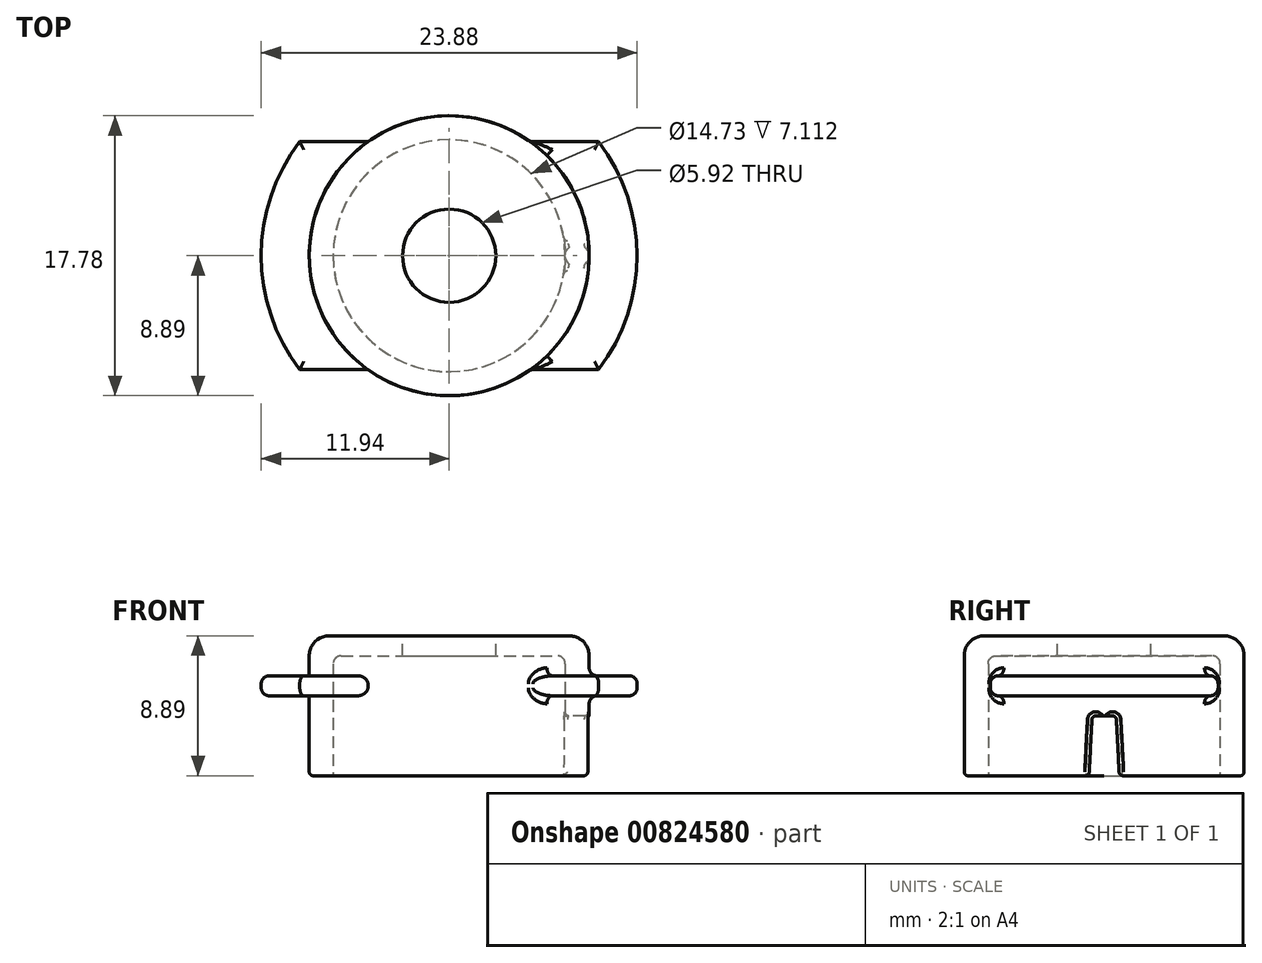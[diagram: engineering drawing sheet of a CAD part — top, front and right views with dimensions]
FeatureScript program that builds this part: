
annotation { "Feature Type Name" : "Feature", "Feature Type Description" : "" }
export const myFeature = defineFeature(function(context is Context, id is Id, definition is map)
    precondition{}
    {
        {
            var Q0;
            Q0=qCreatedBy(makeId("Top.planeOp"),FACE);
            var sketch = newSketch(context, id + "F0", { "sketchPlane" : qUnion([Q0])});
            skCircle(sketch, "E0", {"center": v(0, 0) * mm, "radius": 11.94 * mm});
            skSolve(sketch);
        }
        {
            var Q0;
            Q0=makeQuery(id+"F0.imprint","IMPRINT",FACE,{"disambiguationData":[TD([[makeQuery(id+"F0.imprint","IMPRINT",EDGE,{"derivedFrom":sQuery(id+"F0.wireOp",EDGE,"E0")}),1.0]])]});
            var sketch = newSketch(context, id + "F1", { "sketchPlane" : qUnion([Q0])});
            skLineSegment(sketch, "E1", {"start": v(9.5, 7.24) * mm, "end": v(-9.5, 7.24) * mm});
            skLineSegment(sketch, "E2", {"start": v(9.5, -7.24) * mm, "end": v(-9.5, -7.24) * mm});
            skLineSegment(sketch, "E3", {"start": v(-9.5, 7.24) * mm, "end": v(-9.5, -7.24) * mm, "construction": true});
            skLineSegment(sketch, "E4", {"start": v(9.5, 7.24) * mm, "end": v(9.5, -7.24) * mm, "construction": true});
            skSolve(sketch);
        }
        {
            var Q0;
            Q0=qSketchRegion(id+"F0",true);
            extrude(context, id + "F2", {"entities" : qUnion([Q0]), "depth" : 1.27 * mm, "offsetDistance" : 25.4 * mm});
        }
        {
            var Q0;
            {var subQ0=sQuery(id+"F1.wireOp",EDGE,"E1");Q0=makeQuery(id+"F1.imprint","IMPRINT",FACE,{"disambiguationData":[TD([[makeQuery(id+"F1.imprint","IMPRINT",EDGE,{"derivedFrom":subQ0}),-1.0]])]});}
            var Q1;
            {var subQ0=sQuery(id+"F1.wireOp",EDGE,"E2");Q1=makeQuery(id+"F1.imprint","IMPRINT",FACE,{"disambiguationData":[TD([[makeQuery(id+"F1.imprint","IMPRINT",EDGE,{"derivedFrom":subQ0}),1.0]])]});}
            extrude(context, id + "F3", {"entities" : qUnion([Q0, Q1]), "operationType" : NewBodyOperationType.REMOVE, "depth" : 2.54 * mm, "offsetDistance" : 25.4 * mm, "hasSecondDirection" : true, "secondDirectionOppositeDirection" : true, "secondDirectionDepth" : 25.4 * mm});
        }
        {
            var Q0;
            Q0=makeQuery(id+"F2.opExtrude","CAP_FACE",FACE,{"disambiguationData":[OSD([sQuery(id+"F0.wireOp",EDGE,"E0")])],"isStart":true});
            var sketch = newSketch(context, id + "F4", { "sketchPlane" : qUnion([Q0])});
            skCircle(sketch, "E5", {"center": v(0, 0) * mm, "radius": 8.9 * mm});
            skSolve(sketch);
        }
        {
            var Q0;
            Q0=qSketchRegion(id+"F4",true);
            extrude(context, id + "F5", {"entities" : qUnion([Q0]), "operationType" : NewBodyOperationType.ADD, "oppositeDirection" : true, "depth" : 1.27 * mm, "offsetDistance" : 25.4 * mm});
        }
        {
            var Q0;
            Q0=makeQuery(id+"F5.boolean.opBoolean","MERGE",FACE,{"derivedFrom":[makeQuery(id+"F2.opExtrude","CAP_FACE",FACE,{"disambiguationData":[OSD([sQuery(id+"F0.wireOp",EDGE,"E0")])],"isStart":true}),makeQuery(id+"F5.opExtrude","CAP_FACE",FACE,{"disambiguationData":[OSD([sQuery(id+"F4.wireOp",EDGE,"E5")])],"isStart":true})]});
            var sketch = newSketch(context, id + "F6", { "sketchPlane" : qUnion([Q0])});
            skCircle(sketch, "E6", {"center": v(0, 0) * mm, "radius": 8.9 * mm});
            skSolve(sketch);
        }
        {
            var Q0;
            Q0=qSketchRegion(id+"F6",true);
            extrude(context, id + "F7", {"entities" : qUnion([Q0]), "operationType" : NewBodyOperationType.ADD, "depth" : 5.08 * mm, "offsetDistance" : 25.4 * mm});
        }
        {
            var Q0;
            Q0=makeQuery(id+"F7.opExtrude","CAP_FACE",FACE,{"disambiguationData":[OSD([sQuery(id+"F6.wireOp",EDGE,"E6")])],"isStart":false});
            var sketch = newSketch(context, id + "F8", { "sketchPlane" : qUnion([Q0])});
            skCircle(sketch, "E7", {"center": v(0, 0) * mm, "radius": 7.37 * mm});
            skSolve(sketch);
        }
        {
            var Q0;
            Q0=qSketchRegion(id+"F8",true);
            extrude(context, id + "F9", {"entities" : qUnion([Q0]), "operationType" : NewBodyOperationType.REMOVE, "oppositeDirection" : true, "depth" : 5.08 * mm, "offsetDistance" : 25.4 * mm});
        }
        {
            var Q0;
            Q0=qCreatedBy(makeId("Front.planeOp"),FACE);
            var sketch = newSketch(context, id + "F10", { "sketchPlane" : qUnion([Q0])});
            skLineSegment(sketch, "E8", {"start": v(0, 0) * mm, "end": v(0, -7.62) * mm, "construction": true});
            skSolve(sketch);
        }
        {
            var Q0;
            Q0=makeQuery(id+"F9.boolean.opBoolean","COPY",FACE,{"derivedFrom":makeQuery(id+"F9.opExtrude","CAP_FACE",FACE,{"disambiguationData":[OSD([sQuery(id+"F8.wireOp",EDGE,"E7")])],"isStart":false})});
            var sketch = newSketch(context, id + "F11", { "sketchPlane" : qUnion([Q0])});
            skCircle(sketch, "E9", {"center": v(0, 0) * mm, "radius": 7.37 * mm});
            skSolve(sketch);
        }
        {
            var Q0;
            Q0=makeQuery(id+"F5.boolean.opBoolean","MERGE",FACE,{"derivedFrom":[makeQuery(id+"F2.opExtrude","CAP_FACE",FACE,{"disambiguationData":[OSD([sQuery(id+"F0.wireOp",EDGE,"E0")])],"isStart":false}),makeQuery(id+"F5.opExtrude","CAP_FACE",FACE,{"disambiguationData":[OSD([sQuery(id+"F4.wireOp",EDGE,"E5")])],"isStart":false})]});
            var sketch = newSketch(context, id + "F12", { "sketchPlane" : qUnion([Q0])});
            skCircle(sketch, "E10", {"center": v(0, 0) * mm, "radius": 8.9 * mm});
            skSolve(sketch);
        }
        {
            var Q0;
            Q0=qSketchRegion(id+"F12",true);
            extrude(context, id + "F13", {"entities" : qUnion([Q0]), "operationType" : NewBodyOperationType.ADD, "depth" : 2.54 * mm, "offsetDistance" : 25.4 * mm});
        }
        {
            var Q0;
            Q0=makeQuery(id+"F13.opExtrude","CAP_FACE",FACE,{"disambiguationData":[OSD([sQuery(id+"F12.wireOp",EDGE,"E10")])],"isStart":false});
            var sketch = newSketch(context, id + "F14", { "sketchPlane" : qUnion([Q0])});
            skCircle(sketch, "E11", {"center": v(0, 0) * mm, "radius": 2.96 * mm});
            skSolve(sketch);
        }
        {
            var Q0;
            Q0=qSketchRegion(id+"F14",true);
            extrude(context, id + "F15", {"entities" : qUnion([Q0]), "operationType" : NewBodyOperationType.REMOVE, "oppositeDirection" : true, "depth" : 25.4 * mm, "offsetDistance" : 25.4 * mm, "hasSecondDirection" : true, "secondDirectionOppositeDirection" : false, "secondDirectionDepth" : 25.4 * mm});
        }
        {
            var Q0;
            Q0=makeQuery(id+"F5.boolean.opBoolean","SPLIT",EDGE,{"disambiguationData":[OD(1.0)],"derivedFrom":makeQuery(id+"F3.boolean.opBoolean","INTERSECT",EDGE,{"derivedFrom":[makeQuery(id+"F2.opExtrude","CAP_FACE",FACE,{"disambiguationData":[OSD([sQuery(id+"F0.wireOp",EDGE,"E0")])],"isStart":false}),makeQuery(id+"F3.opExtrude","SWEPT_FACE",FACE,{"disambiguationData":[OSD([sQuery(id+"F1.wireOp",EDGE,"E2")])]})]})});
            var Q1;
            Q1=makeQuery(id+"F5.boolean.opBoolean","SPLIT",EDGE,{"disambiguationData":[OD(1.0)],"derivedFrom":makeQuery(id+"F3.boolean.opBoolean","INTERSECT",EDGE,{"derivedFrom":[makeQuery(id+"F2.opExtrude","CAP_FACE",FACE,{"disambiguationData":[OSD([sQuery(id+"F0.wireOp",EDGE,"E0")])],"isStart":true}),makeQuery(id+"F3.opExtrude","SWEPT_FACE",FACE,{"disambiguationData":[OSD([sQuery(id+"F1.wireOp",EDGE,"E2")])]})]})});
            var Q2;
            Q2=makeQuery(id+"F3.boolean.opBoolean","SPLIT",EDGE,{"disambiguationData":[OD(1.0)],"derivedFrom":makeQuery(id+"F2.opExtrude","CAP_EDGE",EDGE,{"disambiguationData":[OSD([sQuery(id+"F0.wireOp",EDGE,"E0")])],"isStart":true})});
            var Q3;
            Q3=makeQuery(id+"F3.boolean.opBoolean","SPLIT",EDGE,{"disambiguationData":[OD(1.0)],"derivedFrom":makeQuery(id+"F2.opExtrude","CAP_EDGE",EDGE,{"disambiguationData":[OSD([sQuery(id+"F0.wireOp",EDGE,"E0")])],"isStart":false})});
            var Q4;
            Q4=makeQuery(id+"F5.boolean.opBoolean","SPLIT",EDGE,{"disambiguationData":[OD(1.0)],"derivedFrom":makeQuery(id+"F3.boolean.opBoolean","INTERSECT",EDGE,{"derivedFrom":[makeQuery(id+"F2.opExtrude","CAP_FACE",FACE,{"disambiguationData":[OSD([sQuery(id+"F0.wireOp",EDGE,"E0")])],"isStart":true}),makeQuery(id+"F3.opExtrude","SWEPT_FACE",FACE,{"disambiguationData":[OSD([sQuery(id+"F1.wireOp",EDGE,"E1")])]})]})});
            var Q5;
            Q5=makeQuery(id+"F5.boolean.opBoolean","SPLIT",EDGE,{"disambiguationData":[OD(1.0)],"derivedFrom":makeQuery(id+"F3.boolean.opBoolean","INTERSECT",EDGE,{"derivedFrom":[makeQuery(id+"F2.opExtrude","CAP_FACE",FACE,{"disambiguationData":[OSD([sQuery(id+"F0.wireOp",EDGE,"E0")])],"isStart":false}),makeQuery(id+"F3.opExtrude","SWEPT_FACE",FACE,{"disambiguationData":[OSD([sQuery(id+"F1.wireOp",EDGE,"E1")])]})]})});
            var Q6;
            Q6=makeQuery(id+"F5.boolean.opBoolean","SPLIT",EDGE,{"disambiguationData":[OD(0.0)],"derivedFrom":makeQuery(id+"F3.boolean.opBoolean","INTERSECT",EDGE,{"derivedFrom":[makeQuery(id+"F2.opExtrude","CAP_FACE",FACE,{"disambiguationData":[OSD([sQuery(id+"F0.wireOp",EDGE,"E0")])],"isStart":true}),makeQuery(id+"F3.opExtrude","SWEPT_FACE",FACE,{"disambiguationData":[OSD([sQuery(id+"F1.wireOp",EDGE,"E2")])]})]})});
            var Q7;
            Q7=makeQuery(id+"F5.boolean.opBoolean","SPLIT",EDGE,{"disambiguationData":[OD(0.0)],"derivedFrom":makeQuery(id+"F3.boolean.opBoolean","INTERSECT",EDGE,{"derivedFrom":[makeQuery(id+"F2.opExtrude","CAP_FACE",FACE,{"disambiguationData":[OSD([sQuery(id+"F0.wireOp",EDGE,"E0")])],"isStart":false}),makeQuery(id+"F3.opExtrude","SWEPT_FACE",FACE,{"disambiguationData":[OSD([sQuery(id+"F1.wireOp",EDGE,"E2")])]})]})});
            var Q8;
            Q8=makeQuery(id+"F3.boolean.opBoolean","SPLIT",EDGE,{"disambiguationData":[OD(0.0)],"derivedFrom":makeQuery(id+"F2.opExtrude","CAP_EDGE",EDGE,{"disambiguationData":[OSD([sQuery(id+"F0.wireOp",EDGE,"E0")])],"isStart":true})});
            var Q9;
            Q9=makeQuery(id+"F3.boolean.opBoolean","SPLIT",EDGE,{"disambiguationData":[OD(0.0)],"derivedFrom":makeQuery(id+"F2.opExtrude","CAP_EDGE",EDGE,{"disambiguationData":[OSD([sQuery(id+"F0.wireOp",EDGE,"E0")])],"isStart":false})});
            var Q10;
            Q10=makeQuery(id+"F5.boolean.opBoolean","SPLIT",EDGE,{"disambiguationData":[OD(0.0)],"derivedFrom":makeQuery(id+"F3.boolean.opBoolean","INTERSECT",EDGE,{"derivedFrom":[makeQuery(id+"F2.opExtrude","CAP_FACE",FACE,{"disambiguationData":[OSD([sQuery(id+"F0.wireOp",EDGE,"E0")])],"isStart":false}),makeQuery(id+"F3.opExtrude","SWEPT_FACE",FACE,{"disambiguationData":[OSD([sQuery(id+"F1.wireOp",EDGE,"E1")])]})]})});
            var Q11;
            Q11=makeQuery(id+"F5.boolean.opBoolean","SPLIT",EDGE,{"disambiguationData":[OD(0.0)],"derivedFrom":makeQuery(id+"F3.boolean.opBoolean","INTERSECT",EDGE,{"derivedFrom":[makeQuery(id+"F2.opExtrude","CAP_FACE",FACE,{"disambiguationData":[OSD([sQuery(id+"F0.wireOp",EDGE,"E0")])],"isStart":true}),makeQuery(id+"F3.opExtrude","SWEPT_FACE",FACE,{"disambiguationData":[OSD([sQuery(id+"F1.wireOp",EDGE,"E1")])]})]})});
            fillet(context, id + "F16", {"entities" : qUnion([Q0, Q1, Q2, Q3, Q4, Q5, Q6, Q7, Q8, Q9, Q10, Q11]), "radius" : 0.5 * mm, "tangentPropagation" : true, "allowEdgeOverflow" : false});
        }
        {
            var Q0;
            Q0=makeQuery(id+"F13.opExtrude","CAP_EDGE",EDGE,{"disambiguationData":[OSD([sQuery(id+"F12.wireOp",EDGE,"E10")])],"isStart":false});
            fillet(context, id + "F17", {"entities" : qUnion([Q0]), "radius" : 1.27 * mm, "tangentPropagation" : true, "allowEdgeOverflow" : false});
        }
        {
            var Q0;
            Q0=makeQuery(id+"F11.imprint","IMPRINT",FACE,{"disambiguationData":[TD([[makeQuery(id+"F11.imprint","IMPRINT",EDGE,{"derivedFrom":sQuery(id+"F11.wireOp",EDGE,"E9")}),1.0]])]});
            var sketch = newSketch(context, id + "F18", { "sketchPlane" : qUnion([Q0])});
            skCircle(sketch, "E12", {"center": v(0, 0) * mm, "radius": 7.37 * mm});
            skSolve(sketch);
        }
        {
            var Q0;
            Q0=qSketchRegion(id+"F18",true);
            extrude(context, id + "F19", {"entities" : qUnion([Q0]), "operationType" : NewBodyOperationType.REMOVE, "oppositeDirection" : true, "depth" : 2.54 * mm, "offsetDistance" : 25.4 * mm});
        }
        {
            var Q0;
            Q0=makeQuery(id+"F13.opExtrude","CAP_FACE",FACE,{"disambiguationData":[OSD([sQuery(id+"F12.wireOp",EDGE,"E10")])],"isStart":false});
            cPlane(context, id + "F20", {"entities" : qUnion([Q0]), "cplaneType" : CPlaneType.OFFSET, "offset" : 5.08 * mm, "oppositeDirection" : true, "width" : 152.4 * mm, "height" : 152.4 * mm});
        }
        {
            var Q0;
            Q0=qCreatedBy(id+"F20.planeOp",FACE);
            var sketch = newSketch(context, id + "F21", { "sketchPlane" : qUnion([Q0])});
            skLineSegment(sketch, "E13", {"start": v(8.86, 0.76) * mm, "end": v(7.33, 0.76) * mm});
            skLineSegment(sketch, "E14", {"start": v(8.86, -0.76) * mm, "end": v(7.33, -0.76) * mm});
            skLineSegment(sketch, "E15", {"start": v(0, 0) * mm, "end": v(8.9, 0) * mm, "construction": true});
            skArc(sketch, "E16", {"start": v(7.33, 0.76) * mm, "mid": v(7.37, 0) * mm, "end": v(7.33, -0.76) * mm});
            skArc(sketch, "E17", {"start": v(8.86, 0.76) * mm, "mid": v(8.9, 0) * mm, "end": v(8.86, -0.76) * mm});
            skSolve(sketch);
        }
        {
            var Q0;
            Q0=qSketchRegion(id+"F21",true);
            extrude(context, id + "F22", {"entities" : qUnion([Q0]), "operationType" : NewBodyOperationType.REMOVE, "oppositeDirection" : true, "depth" : 25.4 * mm, "offsetDistance" : 25.4 * mm, "hasDraft" : true, "draftAngle" : 3 * degree});
        }
        {
            var Q0;
            Q0=makeQuery(id+"F22.boolean.opBoolean","COPY",EDGE,{"derivedFrom":makeQuery(id+"F22.opExtrude","CAP_EDGE",EDGE,{"disambiguationData":[OSD([sQuery(id+"F21.wireOp",EDGE,"E17")])],"isStart":true})});
            var Q1;
            {var subQ2=sQuery(id+"F4.wireOp",EDGE,"E5");var subQ6=makeQuery(id+"F5.opExtrude","SWEPT_FACE",FACE,{"disambiguationData":[OSD([subQ2])]});Q1=makeQuery(id+"F22.boolean.opBoolean","INTERSECT",EDGE,{"derivedFrom":[makeQuery(id+"F13.boolean.opBoolean","MERGE",FACE,{"derivedFrom":[makeQuery(id+"F7.boolean.opBoolean","MERGE",FACE,{"derivedFrom":[makeQuery(id+"F5.boolean.opBoolean","SPLIT",FACE,{"disambiguationData":[TD([makeQuery(id+"F3.boolean.opBoolean","COPY",FACE,{"derivedFrom":makeQuery(id+"F3.opExtrude","SWEPT_FACE",FACE,{"disambiguationData":[OSD([sQuery(id+"F1.wireOp",EDGE,"E1")])]})})])],"derivedFrom":subQ6}),makeQuery(id+"F5.boolean.opBoolean","SPLIT",FACE,{"disambiguationData":[TD([makeQuery(id+"F3.boolean.opBoolean","COPY",FACE,{"derivedFrom":makeQuery(id+"F3.opExtrude","SWEPT_FACE",FACE,{"disambiguationData":[OSD([sQuery(id+"F1.wireOp",EDGE,"E2")])]})})])],"derivedFrom":subQ6}),makeQuery(id+"F7.opExtrude","SWEPT_FACE",FACE,{"disambiguationData":[OSD([sQuery(id+"F6.wireOp",EDGE,"E6")])]})]}),makeQuery(id+"F13.opExtrude","SWEPT_FACE",FACE,{"disambiguationData":[OSD([sQuery(id+"F12.wireOp",EDGE,"E10")])]})]}),makeQuery(id+"F22.opExtrude","SWEPT_FACE",FACE,{"disambiguationData":[OSD([sQuery(id+"F21.wireOp",EDGE,"E14")])]})]});}
            var Q2;
            {var subQ2=sQuery(id+"F4.wireOp",EDGE,"E5");var subQ6=makeQuery(id+"F5.opExtrude","SWEPT_FACE",FACE,{"disambiguationData":[OSD([subQ2])]});Q2=makeQuery(id+"F22.boolean.opBoolean","INTERSECT",EDGE,{"derivedFrom":[makeQuery(id+"F13.boolean.opBoolean","MERGE",FACE,{"derivedFrom":[makeQuery(id+"F7.boolean.opBoolean","MERGE",FACE,{"derivedFrom":[makeQuery(id+"F5.boolean.opBoolean","SPLIT",FACE,{"disambiguationData":[TD([makeQuery(id+"F3.boolean.opBoolean","COPY",FACE,{"derivedFrom":makeQuery(id+"F3.opExtrude","SWEPT_FACE",FACE,{"disambiguationData":[OSD([sQuery(id+"F1.wireOp",EDGE,"E1")])]})})])],"derivedFrom":subQ6}),makeQuery(id+"F5.boolean.opBoolean","SPLIT",FACE,{"disambiguationData":[TD([makeQuery(id+"F3.boolean.opBoolean","COPY",FACE,{"derivedFrom":makeQuery(id+"F3.opExtrude","SWEPT_FACE",FACE,{"disambiguationData":[OSD([sQuery(id+"F1.wireOp",EDGE,"E2")])]})})])],"derivedFrom":subQ6}),makeQuery(id+"F7.opExtrude","SWEPT_FACE",FACE,{"disambiguationData":[OSD([sQuery(id+"F6.wireOp",EDGE,"E6")])]})]}),makeQuery(id+"F13.opExtrude","SWEPT_FACE",FACE,{"disambiguationData":[OSD([sQuery(id+"F12.wireOp",EDGE,"E10")])]})]}),makeQuery(id+"F22.opExtrude","SWEPT_FACE",FACE,{"disambiguationData":[OSD([sQuery(id+"F21.wireOp",EDGE,"E13")])]})]});}
            var Q3;
            Q3=makeQuery(id+"F22.boolean.opBoolean","INTERSECT",EDGE,{"derivedFrom":[makeQuery(id+"F19.boolean.opBoolean","MERGE",FACE,{"derivedFrom":[makeQuery(id+"F9.boolean.opBoolean","COPY",FACE,{"derivedFrom":makeQuery(id+"F9.opExtrude","SWEPT_FACE",FACE,{"disambiguationData":[OSD([sQuery(id+"F8.wireOp",EDGE,"E7")])]})}),makeQuery(id+"F19.opExtrude","SWEPT_FACE",FACE,{"disambiguationData":[OSD([sQuery(id+"F18.wireOp",EDGE,"E12")])]})]}),makeQuery(id+"F22.opExtrude","SWEPT_FACE",FACE,{"disambiguationData":[OSD([sQuery(id+"F21.wireOp",EDGE,"E14")])]})]});
            var Q4;
            Q4=makeQuery(id+"F22.boolean.opBoolean","INTERSECT",EDGE,{"derivedFrom":[makeQuery(id+"F19.boolean.opBoolean","MERGE",FACE,{"derivedFrom":[makeQuery(id+"F9.boolean.opBoolean","COPY",FACE,{"derivedFrom":makeQuery(id+"F9.opExtrude","SWEPT_FACE",FACE,{"disambiguationData":[OSD([sQuery(id+"F8.wireOp",EDGE,"E7")])]})}),makeQuery(id+"F19.opExtrude","SWEPT_FACE",FACE,{"disambiguationData":[OSD([sQuery(id+"F18.wireOp",EDGE,"E12")])]})]}),makeQuery(id+"F22.opExtrude","SWEPT_FACE",FACE,{"disambiguationData":[OSD([sQuery(id+"F21.wireOp",EDGE,"E13")])]})]});
            var Q5;
            Q5=makeQuery(id+"F22.boolean.opBoolean","COPY",EDGE,{"derivedFrom":makeQuery(id+"F22.opExtrude","CAP_EDGE",EDGE,{"disambiguationData":[OSD([sQuery(id+"F21.wireOp",EDGE,"E16")])],"isStart":true})});
            var Q6;
            Q6=makeQuery(id+"F22.boolean.opBoolean","COPY",EDGE,{"derivedFrom":makeQuery(id+"F22.opExtrude","CAP_EDGE",EDGE,{"disambiguationData":[OSD([sQuery(id+"F21.wireOp",EDGE,"E14")])],"isStart":true})});
            var Q7;
            Q7=makeQuery(id+"F22.boolean.opBoolean","COPY",EDGE,{"derivedFrom":makeQuery(id+"F22.opExtrude","CAP_EDGE",EDGE,{"disambiguationData":[OSD([sQuery(id+"F21.wireOp",EDGE,"E13")])],"isStart":true})});
            var Q8;
            Q8=makeQuery(id+"F22.boolean.opBoolean","INTERSECT",EDGE,{"derivedFrom":[makeQuery(id+"F7.opExtrude","CAP_FACE",FACE,{"disambiguationData":[OSD([sQuery(id+"F6.wireOp",EDGE,"E6")])],"isStart":false}),makeQuery(id+"F22.opExtrude","SWEPT_FACE",FACE,{"disambiguationData":[OSD([sQuery(id+"F21.wireOp",EDGE,"E14")])]})]});
            var Q9;
            Q9=makeQuery(id+"F22.boolean.opBoolean","INTERSECT",EDGE,{"derivedFrom":[makeQuery(id+"F7.opExtrude","CAP_FACE",FACE,{"disambiguationData":[OSD([sQuery(id+"F6.wireOp",EDGE,"E6")])],"isStart":false}),makeQuery(id+"F22.opExtrude","SWEPT_FACE",FACE,{"disambiguationData":[OSD([sQuery(id+"F21.wireOp",EDGE,"E13")])]})]});
            fillet(context, id + "F23", {"entities" : qUnion([Q0, Q1, Q2, Q3, Q4, Q5, Q6, Q7, Q8, Q9]), "radius" : 0.25 * mm, "tangentPropagation" : true, "allowEdgeOverflow" : false});
        }
        {
            var Q0;
            {var subQ1=sQuery(id+"F8.wireOp",EDGE,"E7");Q0=makeQuery(id+"FQYb2V3vegdUbzZ_1.1.F22.boolean.opBoolean","SPLIT",EDGE,{"disambiguationData":[TD([makeQuery(id+"FQYb2V3vegdUbzZ_1.1.F22.opExtrude","SWEPT_FACE",FACE,{"disambiguationData":[OSD([sQuery(id+"F21.wireOp",EDGE,"E13")])]})])],"derivedFrom":makeQuery(id+"F9.boolean.opBoolean","COPY",EDGE,{"derivedFrom":makeQuery(id+"F9.opExtrude","CAP_EDGE",EDGE,{"disambiguationData":[OSD([subQ1])],"isStart":true})})});}
            var Q1;
            {var subQ1=sQuery(id+"F6.wireOp",EDGE,"E6");Q1=makeQuery(id+"FQYb2V3vegdUbzZ_1.1.F22.boolean.opBoolean","SPLIT",EDGE,{"disambiguationData":[TD([makeQuery(id+"FQYb2V3vegdUbzZ_1.1.F22.opExtrude","SWEPT_FACE",FACE,{"disambiguationData":[OSD([sQuery(id+"F21.wireOp",EDGE,"E13")])]})])],"derivedFrom":makeQuery(id+"F7.opExtrude","CAP_EDGE",EDGE,{"disambiguationData":[OSD([subQ1])],"isStart":false})});}
            var Q2;
            {var subQ1=sQuery(id+"F21.wireOp",EDGE,"E14");var subQ3=sQuery(id+"F8.wireOp",EDGE,"E7");var subQ5=sQuery(id+"F21.wireOp",EDGE,"E13");Q2=makeQuery(id+"FQYb2V3vegdUbzZ_1.2.F22.boolean.opBoolean","SPLIT",EDGE,{"disambiguationData":[TD([makeQuery(id+"FQYb2V3vegdUbzZ_1.2.F22.opExtrude","SWEPT_FACE",FACE,{"disambiguationData":[OSD([subQ5])]})])],"derivedFrom":makeQuery(id+"FQYb2V3vegdUbzZ_1.1.F22.boolean.opBoolean","SPLIT",EDGE,{"disambiguationData":[TD([makeQuery(id+"FQYb2V3vegdUbzZ_1.1.F22.opExtrude","SWEPT_FACE",FACE,{"disambiguationData":[OSD([subQ1])]})])],"derivedFrom":makeQuery(id+"F9.boolean.opBoolean","COPY",EDGE,{"derivedFrom":makeQuery(id+"F9.opExtrude","CAP_EDGE",EDGE,{"disambiguationData":[OSD([subQ3])],"isStart":true})})})});}
            var Q3;
            {var subQ2=sQuery(id+"F6.wireOp",EDGE,"E6");var subQ7=sQuery(id+"F21.wireOp",EDGE,"E13");var subQ8=sQuery(id+"F21.wireOp",EDGE,"E14");Q3=makeQuery(id+"FQYb2V3vegdUbzZ_1.2.F22.boolean.opBoolean","SPLIT",EDGE,{"disambiguationData":[TD([makeQuery(id+"FQYb2V3vegdUbzZ_1.2.F22.opExtrude","SWEPT_FACE",FACE,{"disambiguationData":[OSD([subQ7])]})])],"derivedFrom":makeQuery(id+"FQYb2V3vegdUbzZ_1.1.F22.boolean.opBoolean","SPLIT",EDGE,{"disambiguationData":[TD([makeQuery(id+"FQYb2V3vegdUbzZ_1.1.F22.opExtrude","SWEPT_FACE",FACE,{"disambiguationData":[OSD([subQ8])]})])],"derivedFrom":makeQuery(id+"F7.opExtrude","CAP_EDGE",EDGE,{"disambiguationData":[OSD([subQ2])],"isStart":false})})});}
            var Q4;
            {var subQ2=sQuery(id+"F6.wireOp",EDGE,"E6");var subQ4=sQuery(id+"F21.wireOp",EDGE,"E13");var subQ8=sQuery(id+"F21.wireOp",EDGE,"E14");Q4=makeQuery(id+"FQYb2V3vegdUbzZ_1.3.F22.boolean.opBoolean","SPLIT",EDGE,{"disambiguationData":[TD([makeQuery(id+"FQYb2V3vegdUbzZ_1.3.F22.opExtrude","SWEPT_FACE",FACE,{"disambiguationData":[OSD([subQ4])]})])],"derivedFrom":makeQuery(id+"FQYb2V3vegdUbzZ_1.2.F22.boolean.opBoolean","SPLIT",EDGE,{"disambiguationData":[TD([makeQuery(id+"FQYb2V3vegdUbzZ_1.2.F22.opExtrude","SWEPT_FACE",FACE,{"disambiguationData":[OSD([subQ8])]})])],"derivedFrom":makeQuery(id+"FQYb2V3vegdUbzZ_1.1.F22.boolean.opBoolean","SPLIT",EDGE,{"disambiguationData":[TD([makeQuery(id+"FQYb2V3vegdUbzZ_1.1.F22.opExtrude","SWEPT_FACE",FACE,{"disambiguationData":[OSD([subQ8])]})])],"derivedFrom":makeQuery(id+"F7.opExtrude","CAP_EDGE",EDGE,{"disambiguationData":[OSD([subQ2])],"isStart":false})})})});}
            var Q5;
            {var subQ0=sQuery(id+"F21.wireOp",EDGE,"E14");var subQ2=sQuery(id+"F8.wireOp",EDGE,"E7");var subQ6=sQuery(id+"F21.wireOp",EDGE,"E13");Q5=makeQuery(id+"FQYb2V3vegdUbzZ_1.3.F22.boolean.opBoolean","SPLIT",EDGE,{"disambiguationData":[TD([makeQuery(id+"FQYb2V3vegdUbzZ_1.3.F22.opExtrude","SWEPT_FACE",FACE,{"disambiguationData":[OSD([subQ6])]})])],"derivedFrom":makeQuery(id+"FQYb2V3vegdUbzZ_1.2.F22.boolean.opBoolean","SPLIT",EDGE,{"disambiguationData":[TD([makeQuery(id+"FQYb2V3vegdUbzZ_1.2.F22.opExtrude","SWEPT_FACE",FACE,{"disambiguationData":[OSD([subQ0])]})])],"derivedFrom":makeQuery(id+"FQYb2V3vegdUbzZ_1.1.F22.boolean.opBoolean","SPLIT",EDGE,{"disambiguationData":[TD([makeQuery(id+"FQYb2V3vegdUbzZ_1.1.F22.opExtrude","SWEPT_FACE",FACE,{"disambiguationData":[OSD([subQ0])]})])],"derivedFrom":makeQuery(id+"F9.boolean.opBoolean","COPY",EDGE,{"derivedFrom":makeQuery(id+"F9.opExtrude","CAP_EDGE",EDGE,{"disambiguationData":[OSD([subQ2])],"isStart":true})})})})});}
            var Q6;
            {var subQ3=sQuery(id+"F8.wireOp",EDGE,"E7");var subQ6=sQuery(id+"F21.wireOp",EDGE,"E14");Q6=makeQuery(id+"FQYb2V3vegdUbzZ_1.3.F22.boolean.opBoolean","SPLIT",EDGE,{"disambiguationData":[TD([makeQuery(id+"FQYb2V3vegdUbzZ_1.3.F22.opExtrude","SWEPT_FACE",FACE,{"disambiguationData":[OSD([subQ6])]})])],"derivedFrom":makeQuery(id+"FQYb2V3vegdUbzZ_1.2.F22.boolean.opBoolean","SPLIT",EDGE,{"disambiguationData":[TD([makeQuery(id+"FQYb2V3vegdUbzZ_1.2.F22.opExtrude","SWEPT_FACE",FACE,{"disambiguationData":[OSD([subQ6])]})])],"derivedFrom":makeQuery(id+"FQYb2V3vegdUbzZ_1.1.F22.boolean.opBoolean","SPLIT",EDGE,{"disambiguationData":[TD([makeQuery(id+"FQYb2V3vegdUbzZ_1.1.F22.opExtrude","SWEPT_FACE",FACE,{"disambiguationData":[OSD([subQ6])]})])],"derivedFrom":makeQuery(id+"F9.boolean.opBoolean","COPY",EDGE,{"derivedFrom":makeQuery(id+"F9.opExtrude","CAP_EDGE",EDGE,{"disambiguationData":[OSD([subQ3])],"isStart":true})})})})});}
            var Q7;
            {var subQ2=sQuery(id+"F6.wireOp",EDGE,"E6");var subQ8=sQuery(id+"F21.wireOp",EDGE,"E14");Q7=makeQuery(id+"FQYb2V3vegdUbzZ_1.3.F22.boolean.opBoolean","SPLIT",EDGE,{"disambiguationData":[TD([makeQuery(id+"FQYb2V3vegdUbzZ_1.3.F22.opExtrude","SWEPT_FACE",FACE,{"disambiguationData":[OSD([subQ8])]})])],"derivedFrom":makeQuery(id+"FQYb2V3vegdUbzZ_1.2.F22.boolean.opBoolean","SPLIT",EDGE,{"disambiguationData":[TD([makeQuery(id+"FQYb2V3vegdUbzZ_1.2.F22.opExtrude","SWEPT_FACE",FACE,{"disambiguationData":[OSD([subQ8])]})])],"derivedFrom":makeQuery(id+"FQYb2V3vegdUbzZ_1.1.F22.boolean.opBoolean","SPLIT",EDGE,{"disambiguationData":[TD([makeQuery(id+"FQYb2V3vegdUbzZ_1.1.F22.opExtrude","SWEPT_FACE",FACE,{"disambiguationData":[OSD([subQ8])]})])],"derivedFrom":makeQuery(id+"F7.opExtrude","CAP_EDGE",EDGE,{"disambiguationData":[OSD([subQ2])],"isStart":false})})})});}
            fillet(context, id + "F24", {"entities" : qUnion([Q0, Q1, Q2, Q3, Q4, Q5, Q6, Q7]), "radius" : 0.25 * mm, "tangentPropagation" : true, "allowEdgeOverflow" : false});
        }
        {
            var Q0;
            Q0=makeQuery(id+"F19.boolean.opBoolean","COPY",EDGE,{"derivedFrom":makeQuery(id+"F19.opExtrude","CAP_EDGE",EDGE,{"disambiguationData":[OSD([sQuery(id+"F18.wireOp",EDGE,"E12")])],"isStart":false})});
            var Q1;
            Q1=makeQuery(id+"F7.boolean.opBoolean","SPLIT",EDGE,{"disambiguationData":[OD(0.0)],"derivedFrom":makeQuery(id+"F7.opExtrude","CAP_EDGE",EDGE,{"disambiguationData":[OSD([sQuery(id+"F6.wireOp",EDGE,"E6")])],"isStart":true})});
            var Q2;
            Q2=makeQuery(id+"F7.boolean.opBoolean","SPLIT",EDGE,{"disambiguationData":[OD(1.0)],"derivedFrom":makeQuery(id+"F7.opExtrude","CAP_EDGE",EDGE,{"disambiguationData":[OSD([sQuery(id+"F6.wireOp",EDGE,"E6")])],"isStart":true})});
            fillet(context, id + "F25", {"entities" : qUnion([Q0, Q1, Q2]), "radius" : 0.5 * mm, "tangentPropagation" : true, "allowEdgeOverflow" : false});
        }
    });
